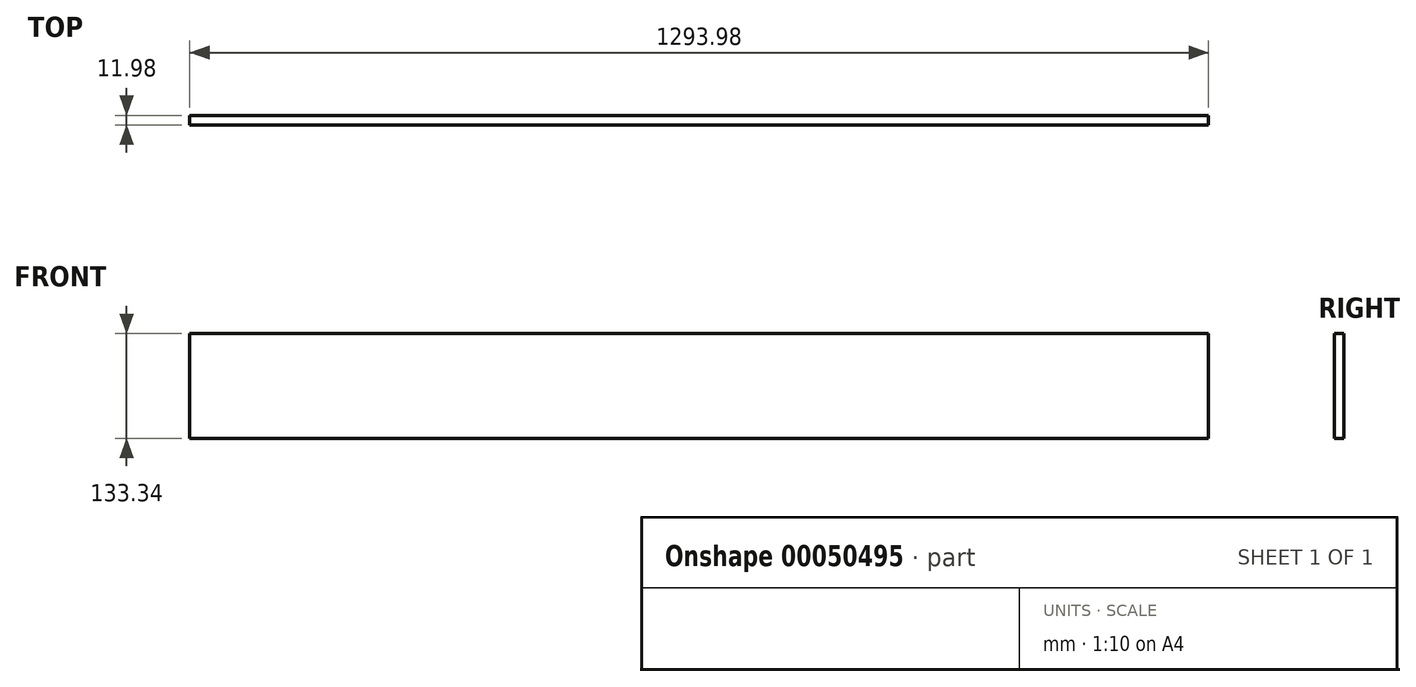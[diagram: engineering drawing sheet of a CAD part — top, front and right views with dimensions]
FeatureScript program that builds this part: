
annotation { "Feature Type Name" : "Feature", "Feature Type Description" : "" }
export const myFeature = defineFeature(function(context is Context, id is Id, definition is map)
    precondition{}
    {
        {
            var Q0;
            Q0=qCreatedBy(makeId("Front.planeOp"),FACE);
            var sketch = newSketch(context, id + "F0", { "sketchPlane" : qUnion([Q0])});
            skLineSegment(sketch, "E0.rect.bottom", {"start": v(646.99, 66.68) * mm, "end": v(-646.99, 66.68) * mm});
            skLineSegment(sketch, "E0.rect.top", {"start": v(646.99, -66.68) * mm, "end": v(-646.99, -66.68) * mm});
            skLineSegment(sketch, "E0.rect.left", {"start": v(646.99, 66.68) * mm, "end": v(646.99, -66.68) * mm});
            skLineSegment(sketch, "E0.rect.right", {"start": v(-646.99, 66.68) * mm, "end": v(-646.99, -66.68) * mm});
            skPoint(sketch, "E0.rect.middle", {"position": v(0, 0) * mm});
            skSolve(sketch);
        }
        {
            var Q0;
            Q0 = qSketchRegion(id + "F0", true);
            extrude(context, id + "F1", {"entities" : qUnion([Q0]), "endBound" : BoundingType.SYMMETRIC, "depth" : 12 * mm});
        }
    });
